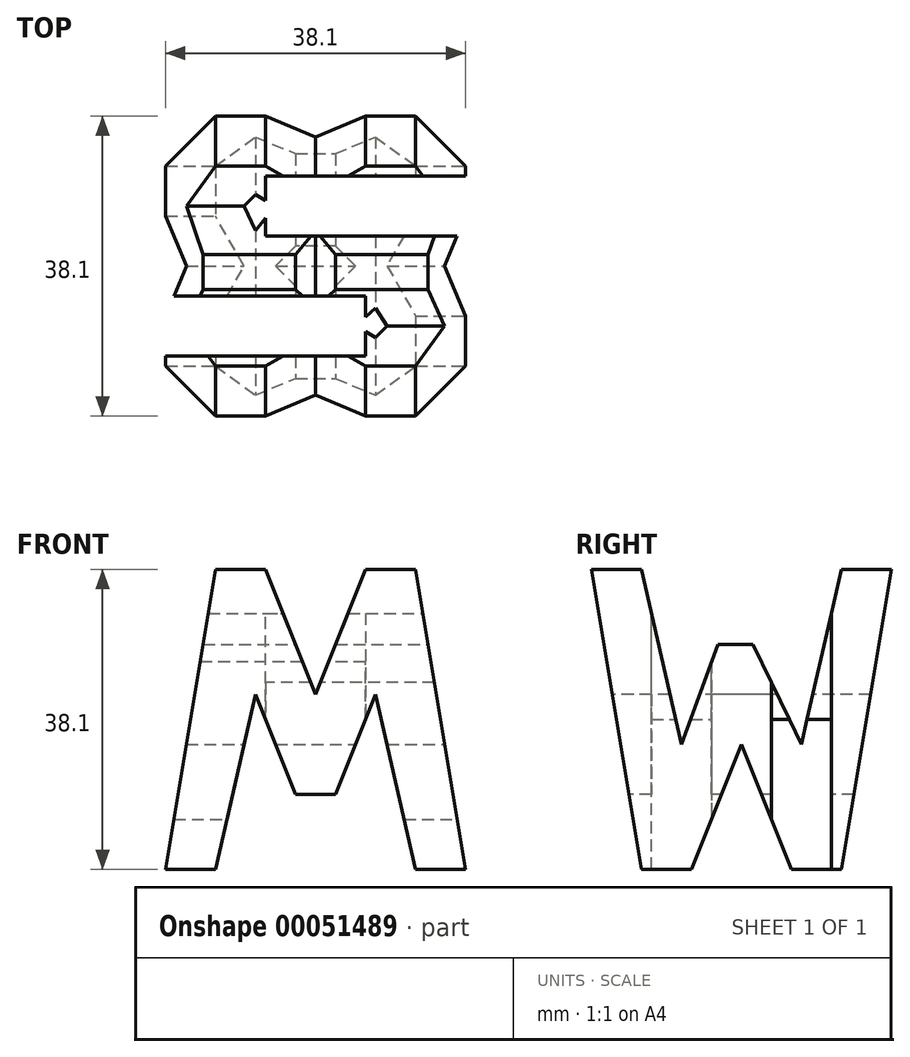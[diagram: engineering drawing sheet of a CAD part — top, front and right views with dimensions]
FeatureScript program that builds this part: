
annotation { "Feature Type Name" : "Feature", "Feature Type Description" : "" }
export const myFeature = defineFeature(function(context is Context, id is Id, definition is map)
    precondition{}
    {
        {
            var Q0;
            Q0=qCreatedBy(makeId("Front.planeOp"),FACE);
            var sketch = newSketch(context, id + "F0", { "sketchPlane" : qUnion([Q0])});
            skLineSegment(sketch, "E0", {"start": v(0, 0) * mm, "end": v(38.1, 0) * mm});
            skLineSegment(sketch, "E1", {"start": v(38.1, 0) * mm, "end": v(38.1, 38.1) * mm});
            skLineSegment(sketch, "E2", {"start": v(38.1, 38.1) * mm, "end": v(0, 38.1) * mm});
            skLineSegment(sketch, "E3", {"start": v(0, 38.1) * mm, "end": v(0, 0) * mm});
            skSolve(sketch);
        }
        {
            var Q0;
            Q0 = qSketchRegion(id + "F0", true);
            extrude(context, id + "F1", {"entities" : qUnion([Q0]), "depth" : 38.1 * mm});
        }
        {
            var Q0;
            Q0=qCreatedBy(makeId("Front.planeOp"),FACE);
            cPlane(context, id + "F2", {"entities" : qUnion([Q0]), "cplaneType" : CPlaneType.OFFSET, "offset" : 38.1 * mm, "width" : 152.4 * mm, "height" : 152.4 * mm});
        }
        {
            var Q0;
            Q0=qCreatedBy(makeId("Right.planeOp"),FACE);
            cPlane(context, id + "F3", {"entities" : qUnion([Q0]), "cplaneType" : CPlaneType.OFFSET, "offset" : 38.1 * mm, "width" : 152.4 * mm, "height" : 152.4 * mm});
        }
        {
            var Q0;
            Q0=qCreatedBy(makeId("Top.planeOp"),FACE);
            cPlane(context, id + "F4", {"entities" : qUnion([Q0]), "cplaneType" : CPlaneType.OFFSET, "offset" : 38.1 * mm, "width" : 152.4 * mm, "height" : 152.4 * mm});
        }
        {
            var Q0;
            Q0=qCreatedBy(id+"F3.planeOp",FACE);
            var sketch = newSketch(context, id + "F5", { "sketchPlane" : qUnion([Q0])});
            skLineSegment(sketch, "E4", {"start": v(0, 0) * mm, "end": v(0, 38.1) * mm});
            skLineSegment(sketch, "E5", {"start": v(0, 38.1) * mm, "end": v(-38.1, 38.1) * mm});
            skLineSegment(sketch, "E6", {"start": v(-38.1, 38.1) * mm, "end": v(-38.1, 0) * mm});
            skLineSegment(sketch, "E7", {"start": v(-38.1, 0) * mm, "end": v(0, 0) * mm});
            skLineSegment(sketch, "E8", {"start": v(-31.75, 38.1) * mm, "end": v(-26.67, 15.87) * mm});
            skLineSegment(sketch, "E9", {"start": v(-26.67, 15.88) * mm, "end": v(-22.06, 28.58) * mm});
            skLineSegment(sketch, "E10", {"start": v(-22.06, 28.58) * mm, "end": v(-17.6, 28.58) * mm});
            skLineSegment(sketch, "E11", {"start": v(-17.6, 28.58) * mm, "end": v(-11.43, 15.88) * mm});
            skLineSegment(sketch, "E12", {"start": v(-11.43, 15.88) * mm, "end": v(-6.35, 38.1) * mm});
            skLineSegment(sketch, "E13", {"start": v(0, 38.1) * mm, "end": v(-6.35, 0) * mm});
            skLineSegment(sketch, "E14", {"start": v(-12.7, 0) * mm, "end": v(-19.05, 15.88) * mm});
            skLineSegment(sketch, "E15", {"start": v(-19.05, 15.88) * mm, "end": v(-25.4, 0) * mm});
            skLineSegment(sketch, "E16", {"start": v(-38.1, 38.1) * mm, "end": v(-31.75, 0) * mm});
            skSolve(sketch);
        }
        {
            var Q0;
            {var subQ0=sQuery(id+"F5.wireOp",EDGE,"E8");Q0=makeQuery(id+"F5.imprint","IMPRINT",FACE,{"disambiguationData":[TD([[makeQuery(id+"F5.imprint","IMPRINT",EDGE,{"derivedFrom":subQ0}),1.0]])]});}
            var Q1;
            {var subQ0=sQuery(id+"F5.wireOp",EDGE,"E6");Q1=makeQuery(id+"F5.imprint","IMPRINT",FACE,{"disambiguationData":[TD([[makeQuery(id+"F5.imprint","IMPRINT",EDGE,{"derivedFrom":subQ0}),1.0]])]});}
            var Q2;
            {var subQ0=sQuery(id+"F5.wireOp",EDGE,"E14");Q2=makeQuery(id+"F5.imprint","IMPRINT",FACE,{"disambiguationData":[TD([[makeQuery(id+"F5.imprint","IMPRINT",EDGE,{"derivedFrom":subQ0}),1.0]])]});}
            var Q3;
            {var subQ0=sQuery(id+"F5.wireOp",EDGE,"E4");Q3=makeQuery(id+"F5.imprint","IMPRINT",FACE,{"disambiguationData":[TD([[makeQuery(id+"F5.imprint","IMPRINT",EDGE,{"derivedFrom":subQ0}),1.0]])]});}
            extrude(context, id + "F6", {"entities" : qUnion([Q0, Q1, Q2, Q3]), "operationType" : NewBodyOperationType.REMOVE, "oppositeDirection" : true, "depth" : 38.1 * mm});
        }
        {
            var Q0;
            Q0=qCreatedBy(id+"F2.planeOp",FACE);
            var sketch = newSketch(context, id + "F7", { "sketchPlane" : qUnion([Q0])});
            skLineSegment(sketch, "E17.bottom", {"start": v(0, 0) * mm, "end": v(38.1, 0) * mm});
            skLineSegment(sketch, "E17.top", {"start": v(0, 38.1) * mm, "end": v(38.1, 38.1) * mm});
            skLineSegment(sketch, "E17.left", {"start": v(0, 0) * mm, "end": v(0, 38.1) * mm});
            skLineSegment(sketch, "E17.right", {"start": v(38.1, 0) * mm, "end": v(38.1, 38.1) * mm});
            skLineSegment(sketch, "E18", {"start": v(0, 0) * mm, "end": v(6.35, 38.1) * mm});
            skLineSegment(sketch, "E19", {"start": v(12.7, 38.1) * mm, "end": v(19.05, 22.22) * mm});
            skLineSegment(sketch, "E20", {"start": v(19.05, 22.22) * mm, "end": v(25.4, 38.1) * mm});
            skLineSegment(sketch, "E21", {"start": v(38.1, 0) * mm, "end": v(31.75, 38.1) * mm});
            skLineSegment(sketch, "E22", {"start": v(6.35, 0) * mm, "end": v(11.43, 22.23) * mm});
            skLineSegment(sketch, "E23", {"start": v(11.43, 22.23) * mm, "end": v(16.51, 9.52) * mm});
            skLineSegment(sketch, "E24", {"start": v(16.51, 9.52) * mm, "end": v(21.6, 9.52) * mm});
            skLineSegment(sketch, "E25", {"start": v(21.6, 9.52) * mm, "end": v(26.67, 22.22) * mm});
            skLineSegment(sketch, "E26", {"start": v(26.67, 22.22) * mm, "end": v(31.75, 0) * mm});
            skSolve(sketch);
        }
        {
            var Q0;
            {var subQ0=sQuery(id+"F7.wireOp",EDGE,"E17.left");Q0=makeQuery(id+"F7.imprint","IMPRINT",FACE,{"disambiguationData":[TD([[makeQuery(id+"F7.imprint","IMPRINT",EDGE,{"derivedFrom":subQ0}),-1.0]])]});}
            var Q1;
            {var subQ0=sQuery(id+"F7.wireOp",EDGE,"E19");Q1=makeQuery(id+"F7.imprint","IMPRINT",FACE,{"disambiguationData":[TD([[makeQuery(id+"F7.imprint","IMPRINT",EDGE,{"derivedFrom":subQ0}),1.0]])]});}
            var Q2;
            {var subQ0=sQuery(id+"F7.wireOp",EDGE,"E22");Q2=makeQuery(id+"F7.imprint","IMPRINT",FACE,{"disambiguationData":[TD([[makeQuery(id+"F7.imprint","IMPRINT",EDGE,{"derivedFrom":subQ0}),-1.0]])]});}
            var Q3;
            {var subQ0=sQuery(id+"F7.wireOp",EDGE,"E17.right");Q3=makeQuery(id+"F7.imprint","IMPRINT",FACE,{"disambiguationData":[TD([[makeQuery(id+"F7.imprint","IMPRINT",EDGE,{"derivedFrom":subQ0}),1.0]])]});}
            extrude(context, id + "F8", {"entities" : qUnion([Q0, Q1, Q2, Q3]), "operationType" : NewBodyOperationType.REMOVE, "oppositeDirection" : true, "depth" : 38.1 * mm});
        }
        {
            var Q0;
            Q0=qCreatedBy(id+"F4.planeOp",FACE);
            var sketch = newSketch(context, id + "F9", { "sketchPlane" : qUnion([Q0])});
            skLineSegment(sketch, "E27.bottom", {"start": v(0, 0) * mm, "end": v(38.1, 0) * mm});
            skLineSegment(sketch, "E27.top", {"start": v(0, -38.1) * mm, "end": v(38.1, -38.1) * mm});
            skLineSegment(sketch, "E27.left", {"start": v(0, 0) * mm, "end": v(0, -38.1) * mm});
            skLineSegment(sketch, "E27.right", {"start": v(38.1, 0) * mm, "end": v(38.1, -38.1) * mm});
            skLineSegment(sketch, "E28", {"start": v(38.1, -7.62) * mm, "end": v(12.7, -7.62) * mm});
            skLineSegment(sketch, "E29", {"start": v(12.7, -7.62) * mm, "end": v(12.7, -15.24) * mm});
            skLineSegment(sketch, "E30", {"start": v(12.7, -15.24) * mm, "end": v(38.1, -15.24) * mm});
            skLineSegment(sketch, "E31", {"start": v(0, -22.86) * mm, "end": v(25.4, -22.86) * mm});
            skLineSegment(sketch, "E32", {"start": v(25.4, -22.86) * mm, "end": v(25.4, -30.48) * mm});
            skLineSegment(sketch, "E33", {"start": v(25.4, -30.48) * mm, "end": v(0, -30.48) * mm});
            skSolve(sketch);
        }
        {
            var Q0;
            {var subQ0=sQuery(id+"F9.wireOp",EDGE,"E28");Q0=makeQuery(id+"F9.imprint","IMPRINT",FACE,{"disambiguationData":[TD([[makeQuery(id+"F9.imprint","IMPRINT",EDGE,{"derivedFrom":subQ0}),1.0]])]});}
            var Q1;
            {var subQ0=sQuery(id+"F9.wireOp",EDGE,"E31");Q1=makeQuery(id+"F9.imprint","IMPRINT",FACE,{"disambiguationData":[TD([[makeQuery(id+"F9.imprint","IMPRINT",EDGE,{"derivedFrom":subQ0}),-1.0]])]});}
            extrude(context, id + "F10", {"entities" : qUnion([Q0, Q1]), "operationType" : NewBodyOperationType.REMOVE, "oppositeDirection" : true, "depth" : 38.1 * mm});
        }
    });
